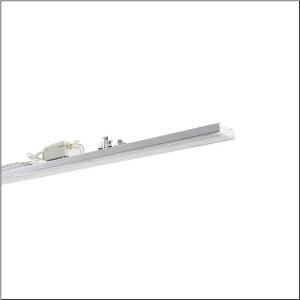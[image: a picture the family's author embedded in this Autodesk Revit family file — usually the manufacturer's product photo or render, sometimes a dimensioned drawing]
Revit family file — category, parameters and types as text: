
# Revit family: licross_r__21_recessed_mo_52tl18mn4a5g_8984
name_source: partatom
category: Lighting Fixtures
units: mm (PartAtom-declared; Revit-internal decimal feet)

## family parameters
Cut with Voids When Loaded = No
Host = Face
Light Source = No
Part Type = Normal
Room Calculation Point = No
Round Connector Dimension = Use Diameter
Shared = No

## types (1)
- --- (1 x LED, 10680 lm, 60.5 W, 4000K)
    Apparent Load = 61 VA
    CIE Flux Codes = 79 95 99 100 100
    Color Rendering = 80
    Color Temperature = 4000K
    Default Elevation = 1800 mm
    Description = Licross® 21 Recessed MO, luminaire insert, of sheet steel, galvanised, coil coated, white, length: 1.500mm, width: 66mm, height: 67mm, LED rated luminous flux: 10.680lm, light colour: 840, control gear: ON/OFF Multilumen, with plug, 3-pole, with phase selection, mains connection: 220..240V, AC, 50/60Hz, rated input power: 61W, halogen-free wiring, primary light control with lens, of plastic, primary optical cover: cover, of PMMA, light emission: direct distribution, primary light characteristic: symmetric, protection rating (complete): IP40, insulation class (complete): insulation class I (protective earthing), certification: CE, ENEC, VDE, UKCA, protection symbol: D if used in an environment without relevant dust loads with corresponding accessories, impact resistance: IK06, permissible ambient temperature for indoor applications: -35..+40°C, corresponds to IFS (International Featured Standards) requirements for safety and quality in the food industry, reducing of maximum allowable ambient temperature of 5°C with ceiling mounting, LABS conformity tested according to VDMA 24364:2018-05, packaging unit: 1 piece
    Height = 58 mm
    Lamp = 1 x LED
    Lamp Light Flux = 10680 lm
    Lamp Power = 60.5 W
    Lamp count = 1
    Length = 1500 mm
    Luminous efficacy = 177 lm/W
    Manufacturer = Siteco
    ModVariant = No
    Model = 52TL18MN4A5G
    Mounting Place = Ceiling
    Mounting Type = Pendant
    Number of Poles = 1
    OnlyDefault = Yes
    Power Factor = 1
    Product Name = Licross® 21 Recessed MO
    Product group = luminaire insert
    ProductGroupID = 901
    Protection Class = Protection class I
    Protection Degree = IP 40
    RLX_Detail_Level = 1
    RLX_Emergency_Light_Flux = 0 lm
    RLX_Emergency_Type = 0
    RLX_Emergency_Type_DB = No
    RlxData = <blob elided: 22229 chars, md5=8323fe1c>
    Socket = socket
    Standby Power = 0 W
    System Light Flux = 10680 lm
    System Power = 61 W
    Type Comments = factory setting: luminous flux: 100 % | (A | C | E) | 140 mA
    Type Image = l_1296930.jpg
    URL = http://relux.com
    VarID = @adj_038129
    Voltage = 0 V
    Weight = 0.00 kg
    Width = 66 mm

## geometry (parser evidence)
native form markers: Blend x4, Sweep x11
no freeform markers — native parametric forms only
